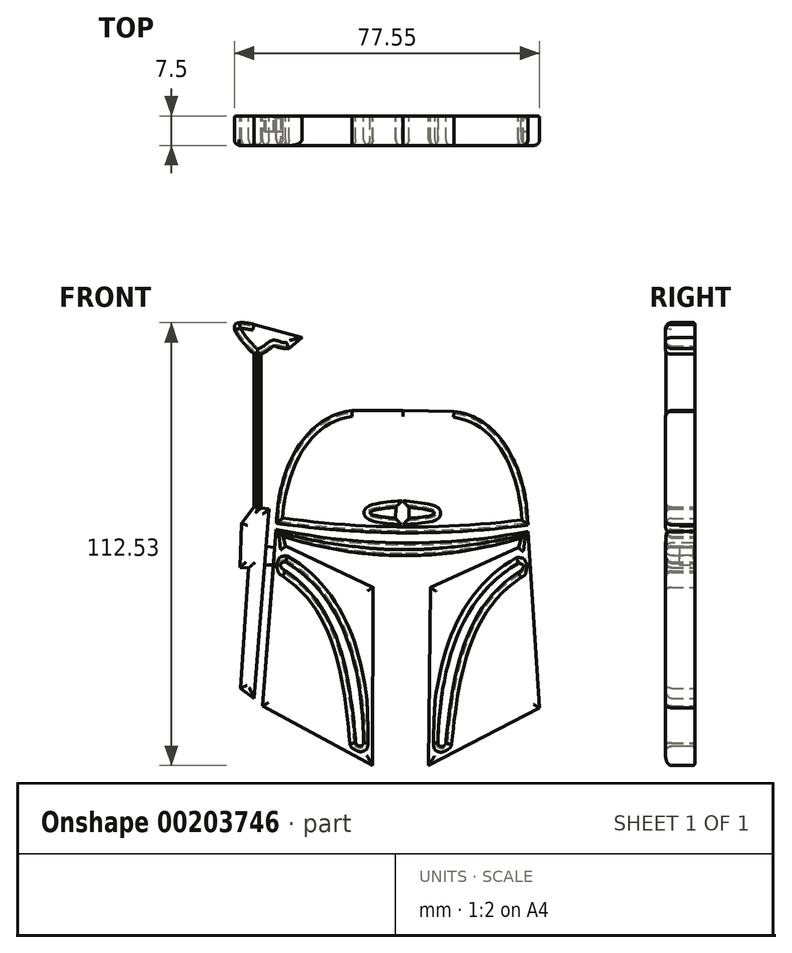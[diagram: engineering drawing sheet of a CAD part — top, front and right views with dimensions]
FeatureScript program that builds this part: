
annotation { "Feature Type Name" : "Feature", "Feature Type Description" : "" }
export const myFeature = defineFeature(function(context is Context, id is Id, definition is map)
    precondition{}
    {
        {
            var Q0;
            Q0=qCreatedBy(makeId("Front.planeOp"),FACE);
            var sketch = newSketch(context, id + "F0", { "sketchPlane" : qUnion([Q0])});
            skLineSegment(sketch, "E0.bottom", {"start": v(-33.97, 33.99) * mm, "end": v(0.15, 33.99) * mm, "construction": true});
            skLineSegment(sketch, "E1", {"start": v(0.2, 40.13) * mm, "end": v(0, 10.78) * mm, "construction": true});
            skPoint(sketch, "E1.endSnap0", {"position": v(0, 10.78) * mm});
            skFitSpline(sketch, "E2", {"points": [v(-32.02, 8.32) * mm, v(32.65, 7.9) * mm], "startDerivative": vector(64.68, -13.38) * mm, "endDerivative": vector(66.5, 13.03) * mm});
            skLineSegment(sketch, "E3", {"start": v(-32.02, 8.32) * mm, "end": v(-35.53, -36.59) * mm});
            skLineSegment(sketch, "E4", {"start": v(-35.53, -36.59) * mm, "end": v(-7.54, -51.63) * mm});
            skLineSegment(sketch, "E5", {"start": v(-7.54, -51.63) * mm, "end": v(-7.36, -6.42) * mm});
            skLineSegment(sketch, "E6", {"start": v(-7.36, -6.42) * mm, "end": v(-29.61, 4.03) * mm});
            skLineSegment(sketch, "E7", {"start": v(-29.61, 4.03) * mm, "end": v(-30.32, 6.49) * mm});
            skFitSpline(sketch, "E8", {"points": [v(-30.32, 6.49) * mm, v(0, 1.63) * mm], "startDerivative": vector(30.75, -9.5) * mm, "endDerivative": vector(30.73, 0) * mm});
            skLineSegment(sketch, "E9.MirrorCS", {"start": v(29.52, 3.65) * mm, "end": v(30.26, 6.1) * mm});
            skFitSpline(sketch, "E10.MirrorCS", {"points": [v(30.26, 6.1) * mm, v(-0.12, 1.63) * mm], "startDerivative": vector(-30.87, -9.1) * mm, "endDerivative": vector(-30.73, 0.4) * mm});
            skLineSegment(sketch, "E11.MirrorCS", {"start": v(7.14, -6.51) * mm, "end": v(29.52, 3.65) * mm});
            skLineSegment(sketch, "E12.MirrorCS", {"start": v(6.73, -51.72) * mm, "end": v(7.14, -6.51) * mm});
            skLineSegment(sketch, "E13.MirrorCS", {"start": v(34.9, -37.05) * mm, "end": v(6.73, -51.72) * mm});
            skLineSegment(sketch, "E14", {"start": v(-33.85, 13.4) * mm, "end": v(-37.6, -34.7) * mm});
            skLineSegment(sketch, "E15", {"start": v(-37.6, -34.7) * mm, "end": v(-41.03, -32.07) * mm});
            skLineSegment(sketch, "E16", {"start": v(-41.03, -32.07) * mm, "end": v(-39.03, -1.55) * mm});
            skLineSegment(sketch, "E17", {"start": v(-39.03, -1.55) * mm, "end": v(-41.23, -1.4) * mm});
            skLineSegment(sketch, "E18", {"start": v(-41.23, -1.4) * mm, "end": v(-40.83, 9.82) * mm});
            skLineSegment(sketch, "E19", {"start": v(-40.83, 9.82) * mm, "end": v(-37.64, 14) * mm});
            skLineSegment(sketch, "E20", {"start": v(-37.64, 14) * mm, "end": v(-33.85, 13.4) * mm});
            skLineSegment(sketch, "E21", {"start": v(-37.64, 8.32) * mm, "end": v(-37.64, 52.8) * mm});
            skLineSegment(sketch, "E22", {"start": v(-37.64, 52.8) * mm, "end": v(-35.82, 52.8) * mm});
            skLineSegment(sketch, "E23", {"start": v(-35.82, 52.8) * mm, "end": v(-35.82, 8.32) * mm});
            skLineSegment(sketch, "E24", {"start": v(-35.82, 8.32) * mm, "end": v(-37.64, 8.32) * mm});
            skFitSpline(sketch, "E25", {"points": [v(-37.64, 52.8) * mm, v(-42.54, 60.2) * mm, v(-37.64, 60.37) * mm], "startDerivative": vector(-17.27, 16.6) * mm, "endDerivative": vector(17.02, -3.75) * mm});
            skLineSegment(sketch, "E26", {"start": v(-37.64, 60.37) * mm, "end": v(-25.48, 57) * mm});
            skLineSegment(sketch, "E27", {"start": v(-25.48, 57) * mm, "end": v(-28.77, 54.26) * mm});
            skFitSpline(sketch, "E28", {"points": [v(-35.82, 52.8) * mm, v(-32.6, 54.88) * mm, v(-28.77, 54.26) * mm], "startDerivative": vector(15.61, 7.7) * mm, "endDerivative": vector(13.71, 1.15) * mm});
            skLineSegment(sketch, "E29.right", {"start": v(-1.7, 11.1) * mm, "end": v(-1.64, 13.9) * mm});
            skPoint(sketch, "E30.1.internal.snap0", {"position": v(-1.67, 12.5) * mm});
            skFitSpline(sketch, "E30", {"points": [v(-1.64, 13.9) * mm, v(-8.26, 12.5) * mm, v(-1.7, 11.1) * mm], "startDerivative": vector(-21.1, -1.32) * mm, "endDerivative": vector(22.52, -1.66) * mm});
            skLineSegment(sketch, "E31.MirrorCS", {"start": v(1.7, 11.08) * mm, "end": v(1.68, 13.88) * mm});
            skFitSpline(sketch, "E32.MirrorCS", {"points": [v(1.68, 13.88) * mm, v(8.28, 12.4) * mm, v(1.7, 11.08) * mm], "startDerivative": vector(21.08, -1.6) * mm, "endDerivative": vector(-22.54, -1.36) * mm});
            skPoint(sketch, "E33.MirrorP", {"position": v(1.7, 12.48) * mm});
            skFitSpline(sketch, "E34", {"points": [v(-9.8, -45.91) * mm, v(-29.61, 0) * mm], "startDerivative": vector(-0.85, 60.77) * mm, "endDerivative": vector(-42.91, 25.07) * mm});
            skFitSpline(sketch, "E35", {"points": [v(-29.61, 0) * mm, v(-29.61, -2.3) * mm], "startDerivative": vector(-5.92, 0) * mm, "endDerivative": vector(4.56, -2.41) * mm});
            skFitSpline(sketch, "E36", {"points": [v(-9.8, -45.91) * mm, v(-11.82, -45.91) * mm], "startDerivative": vector(-0.03, -2.75) * mm, "endDerivative": vector(-1.26, 3.76) * mm});
            skFitSpline(sketch, "E37", {"points": [v(-29.61, -2.3) * mm, v(-11.82, -45.91) * mm], "startDerivative": vector(38.34, -25.62) * mm, "endDerivative": vector(4.88, -60.4) * mm});
            skFitSpline(sketch, "E38.MirrorCS", {"points": [v(9.06, -46.04) * mm, v(29.47, -0.38) * mm], "startDerivative": vector(1.64, 60.75) * mm, "endDerivative": vector(43.23, 24.5) * mm});
            skFitSpline(sketch, "E39.MirrorCS", {"points": [v(29.44, -2.68) * mm, v(11.08, -46.06) * mm], "startDerivative": vector(-38.67, -25.12) * mm, "endDerivative": vector(-5.67, -60.32) * mm});
            skFitSpline(sketch, "E40.MirrorCS", {"points": [v(9.06, -46.04) * mm, v(11.08, -46.06) * mm], "startDerivative": vector(0, -2.75) * mm, "endDerivative": vector(1.3, 3.74) * mm});
            skFitSpline(sketch, "E41.MirrorCS", {"points": [v(29.47, -0.38) * mm, v(29.44, -2.68) * mm], "startDerivative": vector(5.92, -0.08) * mm, "endDerivative": vector(-4.59, -2.35) * mm});
            skLineSegment(sketch, "E42", {"start": v(32, 7.77) * mm, "end": v(34.9, -37.05) * mm});
            skPoint(sketch, "E43.MirrorCS.start.orphan", {"position": v(31.99, 7.9) * mm});
            skFitSpline(sketch, "E44", {"points": [v(-31.92, 9.83) * mm, v(-12.8, 38.45) * mm], "startDerivative": vector(1.05, 39.97) * mm, "endDerivative": vector(37.06, 4.32) * mm});
            skLineSegment(sketch, "E45", {"start": v(-12.8, 38.45) * mm, "end": v(0.18, 38.45) * mm});
            skPoint(sketch, "E46.orphan", {"position": v(0, 38.45) * mm});
            skLineSegment(sketch, "E47.MirrorCS", {"start": v(13.16, 38.28) * mm, "end": v(0.18, 38.45) * mm});
            skFitSpline(sketch, "E48.MirrorCS", {"points": [v(31.9, 9.42) * mm, v(13.16, 38.28) * mm], "startDerivative": vector(-0.53, 39.98) * mm, "endDerivative": vector(-37, 4.8) * mm});
            skFitSpline(sketch, "E49", {"points": [v(-31.92, 9.83) * mm, v(31.9, 9.42) * mm], "startDerivative": vector(64.05, -8.87) * mm, "endDerivative": vector(64.19, 8.89) * mm});
            skSolve(sketch);
        }
        {
            var Q0;
            Q0=makeQuery(id+"F0.imprint","IMPRINT",FACE,{"disambiguationData":[TD([[makeQuery(id+"F0.imprint","IMPRINT",EDGE,{"derivedFrom":sQuery(id+"F0.wireOp",EDGE,"E22")}),1.0]])]});
            var Q1;
            {var subQ5=sQuery(id+"F0.wireOp",EDGE,"E22");Q1=makeQuery(id+"F0.imprint","IMPRINT",FACE,{"disambiguationData":[TD([[makeQuery(id+"F0.imprint","IMPRINT",EDGE,{"derivedFrom":subQ5}),-1.0]])]});}
            var Q2;
            {var subQ5=sQuery(id+"F0.wireOp",EDGE,"E24");Q2=makeQuery(id+"F0.imprint","IMPRINT",FACE,{"disambiguationData":[TD([[makeQuery(id+"F0.imprint","IMPRINT",EDGE,{"derivedFrom":subQ5}),-1.0]])]});}
            var Q3;
            {var subQ5=sQuery(id+"F0.wireOp",EDGE,"E14");Q3=makeQuery(id+"F0.imprint","IMPRINT",FACE,{"disambiguationData":[TD([[makeQuery(id+"F0.imprint","IMPRINT",EDGE,{"derivedFrom":subQ5}),-1.0]])]});}
            var Q4;
            Q4=makeQuery(id+"F0.imprint","IMPRINT",FACE,{"disambiguationData":[TD([[makeQuery(id+"F0.imprint","IMPRINT",EDGE,{"derivedFrom":sQuery(id+"F0.wireOp",EDGE,"5cb4a964-d7a3-414b-8781-b784f41ac383")}),-1.0]])]});
            var Q5;
            {var subQ5=sQuery(id+"F0.wireOp",EDGE,"E3");Q5=makeQuery(id+"F0.imprint","IMPRINT",FACE,{"disambiguationData":[TD([[makeQuery(id+"F0.imprint","IMPRINT",EDGE,{"derivedFrom":subQ5}),1.0]])]});}
            var Q6;
            Q6=makeQuery(id+"F0.imprint","IMPRINT",FACE,{"disambiguationData":[TD([[makeQuery(id+"F0.imprint","IMPRINT",EDGE,{"derivedFrom":sQuery(id+"F0.wireOp",EDGE,"E29.right")}),-1.0]])]});
            extrude(context, id + "F1", {"entities" : qUnion([Q0, Q1, Q2, Q3, Q4, Q5, Q6]), "depth" : 7.5 * mm});
        }
        {
            var Q0;
            Q0=makeQuery(id+"F1.opExtrude","CAP_FACE",FACE,{"disambiguationData":[OSD([sQuery(id+"F0.wireOp",EDGE,"E2"),sQuery(id+"F0.wireOp",EDGE,"E3"),sQuery(id+"F0.wireOp",EDGE,"E4"),sQuery(id+"F0.wireOp",EDGE,"E5"),sQuery(id+"F0.wireOp",EDGE,"E6"),sQuery(id+"F0.wireOp",EDGE,"E7"),sQuery(id+"F0.wireOp",EDGE,"E8"),sQuery(id+"F0.wireOp",EDGE,"E9.MirrorCS"),sQuery(id+"F0.wireOp",EDGE,"E10.MirrorCS"),sQuery(id+"F0.wireOp",EDGE,"E11.MirrorCS"),sQuery(id+"F0.wireOp",EDGE,"E12.MirrorCS"),sQuery(id+"F0.wireOp",EDGE,"E13.MirrorCS"),sQuery(id+"F0.wireOp",EDGE,"E34"),sQuery(id+"F0.wireOp",EDGE,"E35"),sQuery(id+"F0.wireOp",EDGE,"E36"),sQuery(id+"F0.wireOp",EDGE,"E37"),sQuery(id+"F0.wireOp",EDGE,"E38.MirrorCS"),sQuery(id+"F0.wireOp",EDGE,"E39.MirrorCS"),sQuery(id+"F0.wireOp",EDGE,"E40.MirrorCS"),sQuery(id+"F0.wireOp",EDGE,"E41.MirrorCS"),sQuery(id+"F0.wireOp",EDGE,"E42")])],"isStart":false});
            var sketch = newSketch(context, id + "F2", { "sketchPlane" : qUnion([Q0])});
            skFitSpline(sketch, "E50.0.0", {"points": [v(-12.8, 38.45) * mm, v(-25.15, 37) * mm, v(-31.57, 23.16) * mm, v(-31.92, 9.83) * mm]});
            skFitSpline(sketch, "E50.0.1", {"points": [v(-31.92, 9.83) * mm, v(-10.57, 6.87) * mm, v(10.5, 6.46) * mm, v(31.9, 9.42) * mm]});
            skFitSpline(sketch, "E50.0.2", {"points": [v(31.9, 9.42) * mm, v(31.73, 22.75) * mm, v(25.49, 36.68) * mm, v(13.16, 38.28) * mm]});
            skLineSegment(sketch, "E50.0.3", {"start": v(13.16, 38.28) * mm, "end": v(0.18, 38.45) * mm});
            skLineSegment(sketch, "E50.0.4", {"start": v(0.18, 38.45) * mm, "end": v(-12.8, 38.45) * mm});
            skFitSpline(sketch, "E50.1.0", {"points": [v(-37.64, 60.37) * mm, v(-40.05, 60.9) * mm, v(-44.8, 61.28) * mm, v(-40.94, 55.97) * mm, v(-37.64, 52.8) * mm]});
            skLineSegment(sketch, "E50.1.1", {"start": v(-37.64, 52.8) * mm, "end": v(-37.64, 14) * mm});
            skLineSegment(sketch, "E50.1.2", {"start": v(-37.64, 14) * mm, "end": v(-40.83, 9.82) * mm});
            skLineSegment(sketch, "E50.1.3", {"start": v(-40.83, 9.82) * mm, "end": v(-41.23, -1.4) * mm});
            skLineSegment(sketch, "E50.1.4", {"start": v(-41.23, -1.4) * mm, "end": v(-39.03, -1.55) * mm});
            skLineSegment(sketch, "E50.1.5", {"start": v(-39.03, -1.55) * mm, "end": v(-41.03, -32.07) * mm});
            skLineSegment(sketch, "E50.1.6", {"start": v(-41.03, -32.07) * mm, "end": v(-37.6, -34.7) * mm});
            skLineSegment(sketch, "E50.1.7", {"start": v(-37.6, -34.7) * mm, "end": v(-33.85, 13.4) * mm});
            skLineSegment(sketch, "E50.1.8", {"start": v(-33.85, 13.4) * mm, "end": v(-35.82, 13.72) * mm});
            skLineSegment(sketch, "E50.1.9", {"start": v(-35.82, 13.72) * mm, "end": v(-35.82, 52.8) * mm});
            skFitSpline(sketch, "E50.1.10", {"points": [v(-35.82, 52.8) * mm, v(-33.23, 54.07) * mm, v(-33.06, 55.69) * mm, v(-31.06, 54.07) * mm, v(-28.77, 54.26) * mm]});
            skLineSegment(sketch, "E50.1.11", {"start": v(-28.77, 54.26) * mm, "end": v(-25.48, 57) * mm});
            skLineSegment(sketch, "E50.1.12", {"start": v(-25.48, 57) * mm, "end": v(-37.64, 60.37) * mm});
            skPoint(sketch, "E51", {"position": v(-34.58, 3.94) * mm});
            skPoint(sketch, "E52", {"position": v(-34.95, -0.74) * mm});
            skPoint(sketch, "E53", {"position": v(-32.38, 3.74) * mm});
            skPoint(sketch, "E54", {"position": v(-32.73, -0.81) * mm});
            skLineSegment(sketch, "E55", {"start": v(-34.58, 3.94) * mm, "end": v(-32.38, 3.74) * mm});
            skLineSegment(sketch, "E56", {"start": v(-32.38, 3.74) * mm, "end": v(-32.73, -0.81) * mm});
            skLineSegment(sketch, "E57", {"start": v(-34.95, -0.74) * mm, "end": v(-32.73, -0.81) * mm});
            skLineSegment(sketch, "E58", {"start": v(-34.58, 3.94) * mm, "end": v(-34.95, -0.74) * mm});
            skLineSegment(sketch, "E59", {"start": v(-31.92, 9.83) * mm, "end": v(-32.02, 8.32) * mm});
            skLineSegment(sketch, "E60", {"start": v(-30.34, 7.98) * mm, "end": v(-30.23, 9.6) * mm});
            skLineSegment(sketch, "E61", {"start": v(-32.02, 8.32) * mm, "end": v(-30.34, 7.98) * mm});
            skLineSegment(sketch, "E62", {"start": v(32, 7.77) * mm, "end": v(31.9, 9.42) * mm});
            skLineSegment(sketch, "E63", {"start": v(30.26, 7.45) * mm, "end": v(30.16, 9.18) * mm});
            skLineSegment(sketch, "E64", {"start": v(30.26, 7.45) * mm, "end": v(32, 7.77) * mm});
            skLineSegment(sketch, "E65", {"start": v(31.9, 9.42) * mm, "end": v(30.16, 9.18) * mm});
            skSolve(sketch);
        }
        {
            var Q0;
            Q0=makeQuery(id+"F1.opExtrude","CAP_FACE",FACE,{"disambiguationData":[OSD([sQuery(id+"F0.wireOp",EDGE,"E29.right"),sQuery(id+"F0.wireOp",EDGE,"E30"),sQuery(id+"F0.wireOp",EDGE,"E31.MirrorCS"),sQuery(id+"F0.wireOp",EDGE,"E32.MirrorCS"),sQuery(id+"F0.wireOp",EDGE,"E44"),sQuery(id+"F0.wireOp",EDGE,"E45"),sQuery(id+"F0.wireOp",EDGE,"E47.MirrorCS"),sQuery(id+"F0.wireOp",EDGE,"E48.MirrorCS"),sQuery(id+"F0.wireOp",EDGE,"E49")])],"isStart":true});
            var sketch = newSketch(context, id + "F3", { "sketchPlane" : qUnion([Q0])});
            skFitSpline(sketch, "E66.0.0", {"points": [v(-31.9, 9.42) * mm, v(-10.5, 6.46) * mm, v(10.57, 6.87) * mm, v(31.92, 9.83) * mm]});
            skLineSegment(sketch, "E66.0.1", {"start": v(-30.16, 9.18) * mm, "end": v(-30.26, 7.45) * mm});
            skLineSegment(sketch, "E66.0.2", {"start": v(-30.26, 7.45) * mm, "end": v(-32, 7.77) * mm});
            skLineSegment(sketch, "E66.0.3", {"start": v(-32, 7.77) * mm, "end": v(-31.9, 9.42) * mm});
            skFitSpline(sketch, "E66.1.0", {"points": [v(-31.9, 9.42) * mm, v(-10.5, 6.46) * mm, v(10.57, 6.87) * mm, v(31.92, 9.83) * mm]});
            skLineSegment(sketch, "E66.1.1", {"start": v(31.92, 9.83) * mm, "end": v(32.02, 8.32) * mm});
            skLineSegment(sketch, "E66.1.2", {"start": v(32.02, 8.32) * mm, "end": v(30.34, 7.98) * mm});
            skLineSegment(sketch, "E66.1.3", {"start": v(30.34, 7.98) * mm, "end": v(30.23, 9.6) * mm});
            skLineSegment(sketch, "E66.2.0", {"start": v(32.38, 3.74) * mm, "end": v(34.58, 3.94) * mm});
            skLineSegment(sketch, "E66.2.1", {"start": v(34.58, 3.94) * mm, "end": v(34.95, -0.74) * mm});
            skLineSegment(sketch, "E66.2.2", {"start": v(34.95, -0.74) * mm, "end": v(32.73, -0.81) * mm});
            skLineSegment(sketch, "E66.2.3", {"start": v(32.73, -0.81) * mm, "end": v(32.38, 3.74) * mm});
            skSolve(sketch);
        }
        {
            var Q0;
            Q0=makeQuery(id+"F1.opExtrude","CAP_FACE",FACE,{"disambiguationData":[OSD([sQuery(id+"F0.wireOp",EDGE,"E29.right"),sQuery(id+"F0.wireOp",EDGE,"E30"),sQuery(id+"F0.wireOp",EDGE,"E31.MirrorCS"),sQuery(id+"F0.wireOp",EDGE,"E32.MirrorCS"),sQuery(id+"F0.wireOp",EDGE,"E44"),sQuery(id+"F0.wireOp",EDGE,"E45"),sQuery(id+"F0.wireOp",EDGE,"E47.MirrorCS"),sQuery(id+"F0.wireOp",EDGE,"E48.MirrorCS"),sQuery(id+"F0.wireOp",EDGE,"E49")])],"isStart":false});
            var Q1;
            Q1=makeQuery(id+"F1.opExtrude","CAP_FACE",FACE,{"disambiguationData":[OSD([sQuery(id+"F0.wireOp",EDGE,"E2"),sQuery(id+"F0.wireOp",EDGE,"E3"),sQuery(id+"F0.wireOp",EDGE,"E4"),sQuery(id+"F0.wireOp",EDGE,"E5"),sQuery(id+"F0.wireOp",EDGE,"E6"),sQuery(id+"F0.wireOp",EDGE,"E7"),sQuery(id+"F0.wireOp",EDGE,"E8"),sQuery(id+"F0.wireOp",EDGE,"E9.MirrorCS"),sQuery(id+"F0.wireOp",EDGE,"E10.MirrorCS"),sQuery(id+"F0.wireOp",EDGE,"E11.MirrorCS"),sQuery(id+"F0.wireOp",EDGE,"E12.MirrorCS"),sQuery(id+"F0.wireOp",EDGE,"E13.MirrorCS"),sQuery(id+"F0.wireOp",EDGE,"E34"),sQuery(id+"F0.wireOp",EDGE,"E35"),sQuery(id+"F0.wireOp",EDGE,"E36"),sQuery(id+"F0.wireOp",EDGE,"E37"),sQuery(id+"F0.wireOp",EDGE,"E38.MirrorCS"),sQuery(id+"F0.wireOp",EDGE,"E39.MirrorCS"),sQuery(id+"F0.wireOp",EDGE,"E40.MirrorCS"),sQuery(id+"F0.wireOp",EDGE,"E41.MirrorCS"),sQuery(id+"F0.wireOp",EDGE,"E42")])],"isStart":false});
            var Q2;
            Q2=makeQuery(id+"F1.opExtrude","CAP_FACE",FACE,{"disambiguationData":[OSD([sQuery(id+"F0.wireOp",EDGE,"E14"),sQuery(id+"F0.wireOp",EDGE,"E15"),sQuery(id+"F0.wireOp",EDGE,"E16"),sQuery(id+"F0.wireOp",EDGE,"E17"),sQuery(id+"F0.wireOp",EDGE,"E18"),sQuery(id+"F0.wireOp",EDGE,"E19"),sQuery(id+"F0.wireOp",EDGE,"E20"),sQuery(id+"F0.wireOp",EDGE,"E21"),sQuery(id+"F0.wireOp",EDGE,"E23"),sQuery(id+"F0.wireOp",EDGE,"E25"),sQuery(id+"F0.wireOp",EDGE,"E26"),sQuery(id+"F0.wireOp",EDGE,"E27"),sQuery(id+"F0.wireOp",EDGE,"E28")])],"isStart":false});
            fillet(context, id + "F4", {"entities" : qUnion([Q0, Q1, Q2]), "radius" : 1.5 * mm, "tangentPropagation" : true, "allowEdgeOverflow" : false});
        }
        {
            var Q0;
            Q0=makeQuery(id+"F1.opExtrude","CAP_FACE",FACE,{"disambiguationData":[OSD([sQuery(id+"F0.wireOp",EDGE,"E14"),sQuery(id+"F0.wireOp",EDGE,"E15"),sQuery(id+"F0.wireOp",EDGE,"E16"),sQuery(id+"F0.wireOp",EDGE,"E17"),sQuery(id+"F0.wireOp",EDGE,"E18"),sQuery(id+"F0.wireOp",EDGE,"E19"),sQuery(id+"F0.wireOp",EDGE,"E20"),sQuery(id+"F0.wireOp",EDGE,"E21"),sQuery(id+"F0.wireOp",EDGE,"E23"),sQuery(id+"F0.wireOp",EDGE,"E25"),sQuery(id+"F0.wireOp",EDGE,"E26"),sQuery(id+"F0.wireOp",EDGE,"E27"),sQuery(id+"F0.wireOp",EDGE,"E28")])],"isStart":true});
            var Q1;
            Q1=makeQuery(id+"F1.opExtrude","CAP_FACE",FACE,{"disambiguationData":[OSD([sQuery(id+"F0.wireOp",EDGE,"E2"),sQuery(id+"F0.wireOp",EDGE,"E3"),sQuery(id+"F0.wireOp",EDGE,"E4"),sQuery(id+"F0.wireOp",EDGE,"E5"),sQuery(id+"F0.wireOp",EDGE,"E6"),sQuery(id+"F0.wireOp",EDGE,"E7"),sQuery(id+"F0.wireOp",EDGE,"E8"),sQuery(id+"F0.wireOp",EDGE,"E9.MirrorCS"),sQuery(id+"F0.wireOp",EDGE,"E10.MirrorCS"),sQuery(id+"F0.wireOp",EDGE,"E11.MirrorCS"),sQuery(id+"F0.wireOp",EDGE,"E12.MirrorCS"),sQuery(id+"F0.wireOp",EDGE,"E13.MirrorCS"),sQuery(id+"F0.wireOp",EDGE,"E34"),sQuery(id+"F0.wireOp",EDGE,"E35"),sQuery(id+"F0.wireOp",EDGE,"E36"),sQuery(id+"F0.wireOp",EDGE,"E37"),sQuery(id+"F0.wireOp",EDGE,"E38.MirrorCS"),sQuery(id+"F0.wireOp",EDGE,"E39.MirrorCS"),sQuery(id+"F0.wireOp",EDGE,"E40.MirrorCS"),sQuery(id+"F0.wireOp",EDGE,"E41.MirrorCS"),sQuery(id+"F0.wireOp",EDGE,"E42")])],"isStart":true});
            var Q2;
            Q2=makeQuery(id+"F1.opExtrude","CAP_FACE",FACE,{"disambiguationData":[OSD([sQuery(id+"F0.wireOp",EDGE,"E29.right"),sQuery(id+"F0.wireOp",EDGE,"E30"),sQuery(id+"F0.wireOp",EDGE,"E31.MirrorCS"),sQuery(id+"F0.wireOp",EDGE,"E32.MirrorCS"),sQuery(id+"F0.wireOp",EDGE,"E44"),sQuery(id+"F0.wireOp",EDGE,"E45"),sQuery(id+"F0.wireOp",EDGE,"E47.MirrorCS"),sQuery(id+"F0.wireOp",EDGE,"E48.MirrorCS"),sQuery(id+"F0.wireOp",EDGE,"E49")])],"isStart":true});
            var Q3;
            Q3=makeQuery(id+"F1.opExtrude","CAP_EDGE",EDGE,{"disambiguationData":[OSD([sQuery(id+"F0.wireOp",EDGE,"E37")])],"isStart":true});
            fillet(context, id + "F5", {"entities" : qUnion([Q0, Q1, Q2, Q3]), "radius" : .5 * mm, "tangentPropagation" : true, "allowEdgeOverflow" : false});
        }
        {
            var Q0;
            Q0=makeQuery(id+"F3.imprint","IMPRINT",FACE,{"disambiguationData":[TD([[makeQuery(id+"F3.imprint","IMPRINT",EDGE,{"derivedFrom":sQuery(id+"F3.wireOp",EDGE,"E66.2.0")}),-1.0]])]});
            var Q1;
            Q1=makeQuery(id+"F3.imprint","IMPRINT",FACE,{"disambiguationData":[TD([[makeQuery(id+"F3.imprint","IMPRINT",EDGE,{"derivedFrom":sQuery(id+"F3.wireOp",EDGE,"E66.1.0")}),1.0]])]});
            var Q2;
            Q2=makeQuery(id+"F3.imprint","IMPRINT",FACE,{"disambiguationData":[TD([[makeQuery(id+"F3.imprint","IMPRINT",EDGE,{"derivedFrom":sQuery(id+"F3.wireOp",EDGE,"E66.0.0")}),1.0]])]});
            extrude(context, id + "F6", {"entities" : qUnion([Q0, Q1, Q2]), "operationType" : NewBodyOperationType.ADD, "oppositeDirection" : true, "depth" : 4 * mm});
        }
    });
